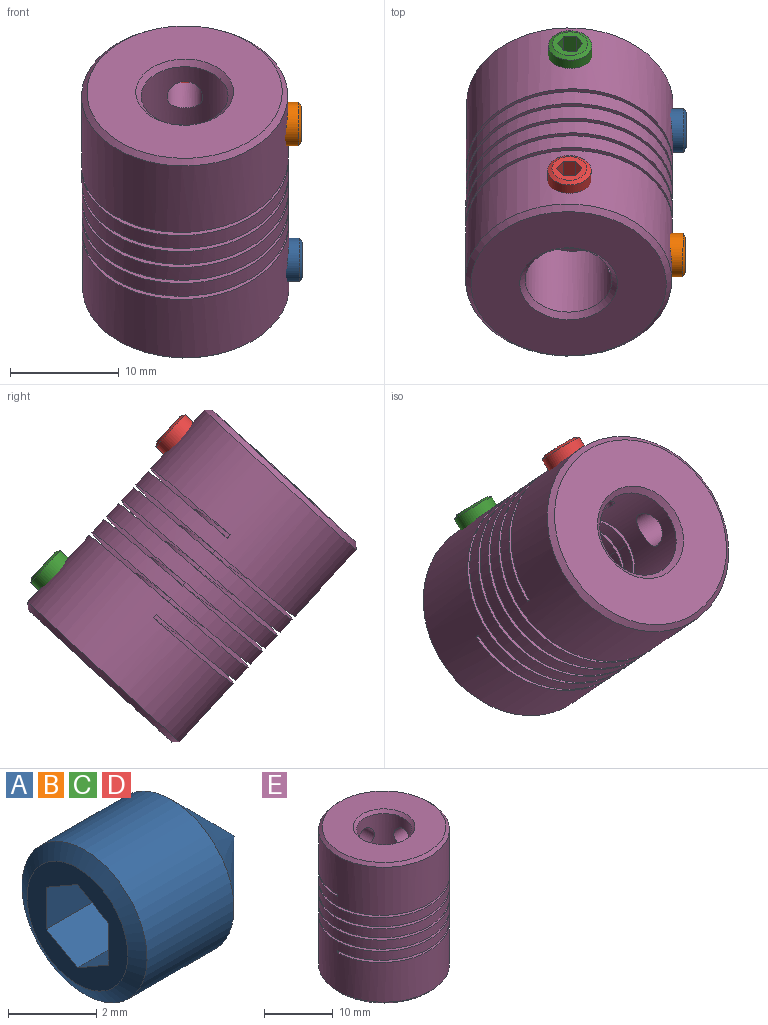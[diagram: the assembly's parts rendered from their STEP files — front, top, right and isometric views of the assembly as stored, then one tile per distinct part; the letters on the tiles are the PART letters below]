
ASSEMBLY  parts=5 mates=4
PART A: 12 faces, bbox 5x4x4 mm
  f0: cone r=1.61mm half-angle=60deg, axis (1,0,0), area 5.1mm2, adj f1,f3
  f1: cylinder r=2mm len=4mm, axis (-1,0,0), area 34.9mm2, adj f0,f2
  f2: cone r=2mm half-angle=45deg, axis (-1,0,0), area 17.8mm2, adj f1,f4
  f3: plane 3.22x3.22mm, normal (-1,0,0), area 4.7mm2, adj f0,f5,f6,f7,f8,f9,f10
  f4: plane 0.01x0.01mm, normal (1,0,0), area 0mm2, adj f2
  f5: plane 2.5x1mm, normal (0,-0.5,-0.87), area 2.9mm2, adj f3,f6,f10,f11
  f6: plane 2.5x1mm, normal (0,0.5,-0.87), area 2.9mm2, adj f3,f5,f7,f11
  f7: plane 2.5x1.15mm, normal (0,1,0), area 2.9mm2, adj f3,f6,f8,f11
  f8: plane 2.5x1mm, normal (0,0.5,0.87), area 2.9mm2, adj f3,f7,f9,f11
  f9: plane 2.5x1mm, normal (0,-0.5,0.87), area 2.9mm2, adj f3,f8,f10,f11
  f10: plane 2.5x1.15mm, normal (0,-1,0), area 2.9mm2, adj f3,f5,f9,f11
  f11: plane 2.31x2mm, normal (-1,0,0), area 3.5mm2, adj f5,f6,f7,f8,f9,f10
PART B: same geometry as A
PART C: same geometry as A
PART D: same geometry as A
PART E: 32 faces, bbox 20.3x21.3x25 mm
  f0: cylinder r=1.65mm len=6.43mm, axis (1,-0.01,0), area 64.1mm2, adj f1,f12
  f1: cone r=2.02mm half-angle=45deg, axis (1,-0.01,0), area 4.5mm2, adj f0,f20
  f2: cylinder r=1.65mm len=6.43mm, axis (0.01,1,0), area 66.5mm2, adj f3,f12
  f3: cone r=2.02mm half-angle=45deg, axis (0.01,1,0), area 4.5mm2, adj f2,f20
  f4: cylinder r=1.65mm len=5.5mm, axis (1,-0.01,0), area 55mm2, adj f5,f14
  f5: cone r=2.02mm half-angle=45deg, axis (1,-0.01,0), area 4.5mm2, adj f4,f24
  f6: cylinder r=1.65mm len=5.5mm, axis (0.01,1,0), area 56.8mm2, adj f7,f14
  f7: cone r=2.02mm half-angle=45deg, axis (0.01,1,0), area 4.5mm2, adj f6,f24
  f8: cone r=9mm half-angle=45deg, axis (0,0,-1), area 41.1mm2, adj f24,f25
  f9: cone r=4mm half-angle=45deg, axis (0,0,1), area 18.9mm2, adj f14,f25
  f10: cone r=9.5mm half-angle=45deg, axis (0,0,1), area 41.1mm2, adj f20,f26
  f11: cone r=3.17mm half-angle=45deg, axis (0,0,-1), area 15.2mm2, adj f12,f26
  f12: cylinder r=3.17mm len=7.5mm, axis (0,0,-1), area 129.4mm2, adj f0,f2,f11,f13,f27,f28,f31
  f13: cylinder r=3.17mm len=2.57mm, axis (0,0,-1), area 0.4mm2, adj f12,f27,f30
  f14: cylinder r=4mm len=9.8mm, axis (0,0,-1), area 198.7mm2, adj f4,f6,f9,f15,f29,f30,f31
  f15: cylinder r=4mm len=8mm, axis (0,0,-1), area 40.2mm2, adj f14,f16,f30,f31
  f16: cylinder r=4mm len=8mm, axis (0,0,-1), area 40.2mm2, adj f15,f17,f30,f31
  f17: cylinder r=4mm len=8mm, axis (0,0,-1), area 40.2mm2, adj f16,f18,f30,f31
  f18: cylinder r=4mm len=8mm, axis (0,0,-1), area 29.6mm2, adj f17,f19,f27,f30,f31
  f19: cylinder r=4mm len=3.24mm, axis (0,0,-1), area 0.6mm2, adj f18,f27,f31
  f20: cylinder r=9.5mm len=19mm, axis (0,0,-1), area 489.8mm2, adj f1,f3,f10,f21,f28,f30,f31
  f21: cylinder r=9.5mm len=19mm, axis (0,0,-1), area 95.5mm2, adj f20,f22,f30,f31
  f22: cylinder r=9.5mm len=19mm, axis (0,0,-1), area 95.5mm2, adj f21,f23,f30,f31
  f23: cylinder r=9.5mm len=19mm, axis (0,0,-1), area 95.5mm2, adj f22,f24,f30,f31
  f24: cylinder r=9.5mm len=19mm, axis (0,0,-1), area 489.8mm2, adj f5,f7,f8,f23,f29,f30,f31
  f25: plane 18x18mm, normal (0,0,1), area 190.9mm2, adj f8,f9
  f26: plane 18x18mm, normal (0,0,-1), area 212mm2, adj f10,f11
  f27: plane 8x7.24mm, normal (0,0,1), area 14.9mm2, adj f12,f13,f18,f19,f30,f31
  f28: plane 6.33x0.4mm, normal (0,-1,0), area 2.5mm2, adj f12,f20,f30,f31
  f29: plane 5.5x0.4mm, normal (0,1,0), area 2.2mm2, adj f14,f24,f30,f31
  f30: bspline ~21.31x20.27mm, area 1170.5mm2, adj f13,f14,f15,f16,f17,f18,f20,f21
  f31: bspline ~21.31x20.27mm, area 1174.2mm2, adj f12,f14,f15,f16,f17,f18,f19,f20
PLACE A rot(axis=(0,-0.36,0.93),179.6deg) t=(15.1,-3.9,-4.81)mm
PLACE B rot(axis=(0,-0.92,0.4),179.8deg) t=(15.02,-15.41,7.7)mm
PLACE C rot(axis=(0.67,-0.3,-0.68),147.3deg) t=(4.42,4.08,2.47)mm
PLACE D rot(axis=(0.67,-0.3,-0.68),147.3deg) t=(4.34,-7.44,14.98)mm
PLACE E rot(axis=(1,-0.01,0),42.6deg) t=(4.32,-9.58,1.45)mm
MATE fastened D.f0 <-> E.f6  axis (0,0.74,0.68) through (4.33,-8.63,13.88)mm
MATE fastened C.f0 <-> E.f2  axis (0,0.74,0.68) through (4.41,2.89,1.37)mm
MATE fastened B.f0 <-> E.f4  axis (1,-0.01,0) through (13.41,-15.4,7.7)mm
MATE fastened E.f0 <-> A.f0  axis (1,-0.01,0) through (13.49,-3.89,-4.81)mm
